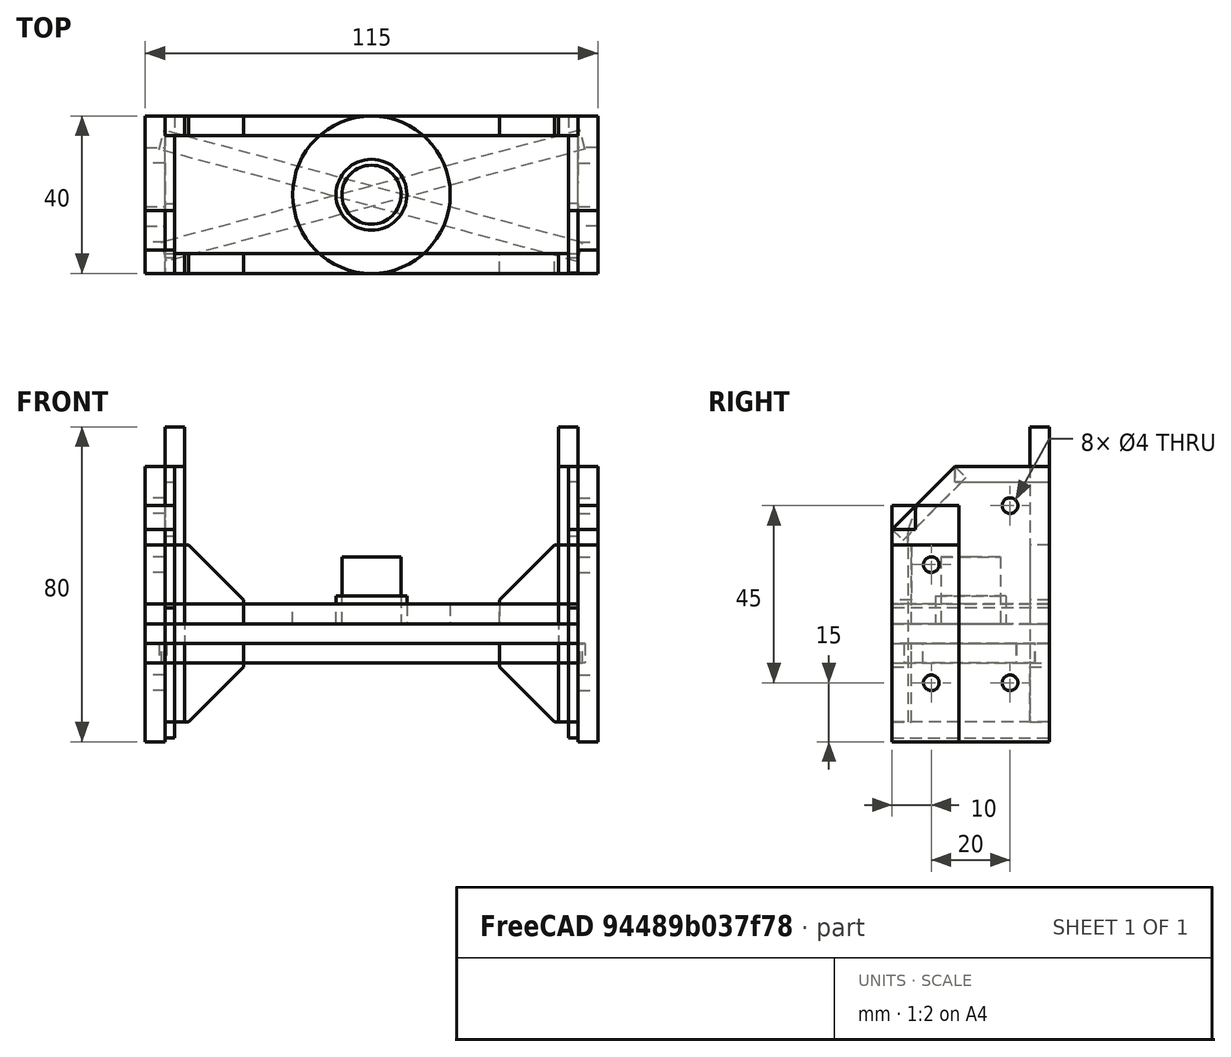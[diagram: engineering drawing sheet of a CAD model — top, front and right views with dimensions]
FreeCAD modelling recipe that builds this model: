
FCSTD DOCUMENT  (FreeCAD 0.20R29410 (Git))
Label: middle_01
License: All rights reserved
LicenseURL: http://en.wikipedia.org/wiki/All_rights_reserved
objects: Part::Extrusion×64, Part::Part2DObjectPython×61, Part::Cut×14, Part::Chamfer×13, Part::FeaturePython×6, Part::MultiFuse×4, App::FeaturePython×2
note: 162 computed .brp shape members not serialized (recipe doc carries the construction recipe); baked Part::Feature solids carry a one-line shape summary decoded from their .brp

FEATURE [Part::Part2DObjectPython] Rectangle003  # Draft 2D object (typed FeaturePython)
  Area = 0
  ChamferSize = 0
  Columns = 1
  FilletRadius = 0
  Height = 60
  Length = 17
  MakeFace = false
  Placement = pos=(0,0,10) rot=(0.57735,0.57735,0.57735;2.0944rad)
  Rows = 1
FEATURE [Part::Extrusion] Extrude002
  Base = -> Rectangle003
  Dir = (1,0,0)
  DirMode = 2
  FaceMakerClass = Part::FaceMakerBullseye
  LengthFwd = 5
  LengthRev = 0
  Placement = pos=(-140,0,0) rot=(0,0,1;0rad)
  Solid = true
  Symmetric = false
FEATURE [Part::Part2DObjectPython] Rectangle025  # Draft 2D object (typed FeaturePython)
  Area = 0
  ChamferSize = 0
  Columns = 1
  FilletRadius = 0
  Height = 60
  Length = 23
  MakeFace = false
  Placement = pos=(0,17,10) rot=(0.57735,0.57735,0.57735;2.0944rad)
  Rows = 1
FEATURE [Part::Extrusion] Extrude018
  Base = -> Rectangle025
  Dir = (1,-2e-16,2e-16)
  DirMode = 2
  FaceMakerClass = Part::FaceMakerBullseye
  LengthFwd = 5
  LengthRev = 0
  Placement = pos=(-140,0,0) rot=(0,0,1;0rad)
  Solid = true
  Symmetric = false
FEATURE [Part::Part2DObjectPython] Rectangle026  # Draft 2D object (typed FeaturePython)
  Area = 0
  ChamferSize = 0
  Columns = 1
  FilletRadius = 0
  Height = 20
  Length = 23
  MakeFace = false
  Placement = pos=(0,17,70) rot=(0.57735,0.57735,0.57735;2.0944rad)
  Rows = 1
FEATURE [Part::Extrusion] Extrude019
  Base = -> Rectangle026
  Dir = (1,-2e-16,2e-16)
  DirMode = 2
  FaceMakerClass = Part::FaceMakerBullseye
  LengthFwd = 5
  LengthRev = 0
  Placement = pos=(0,-17,0) rot=(0,0,1;0rad)
  Solid = true
  Symmetric = false
FEATURE [Part::Chamfer] Chamfer006
  Base = -> Extrude019
  Edges = 1 edges r=16: [Edge8]
  Placement = pos=(-140,0,0) rot=(0,0,1;0rad)
FEATURE [Part::Part2DObjectPython] Rectangle027  # Draft 2D object (typed FeaturePython)
  Area = 0
  ChamferSize = 0
  Columns = 1
  FilletRadius = 0
  Height = 20
  Length = 17
  MakeFace = false
  Placement = pos=(0,0,70) rot=(0.57735,0.57735,0.57735;2.0944rad)
  Rows = 1
FEATURE [Part::Extrusion] Extrude020
  Base = -> Rectangle027
  Dir = (1,-2e-16,2e-16)
  DirMode = 2
  FaceMakerClass = Part::FaceMakerBullseye
  LengthFwd = 5
  LengthRev = 0
  Placement = pos=(-140,23,0) rot=(0,0,1;0rad)
  Solid = true
  Symmetric = false
FEATURE [Part::Part2DObjectPython] Rectangle029  # Draft 2D object (typed FeaturePython)
  Area = 0
  ChamferSize = 0
  Columns = 1
  FilletRadius = 0
  Height = 4
  Length = 24
  MakeFace = false
  Placement = pos=(5,16,86) rot=(0.57735,0.57735,0.57735;2.0944rad)
  Rows = 1
FEATURE [Part::Part2DObjectPython] Rectangle028  # Draft 2D object (typed FeaturePython)
  Area = 0
  ChamferSize = 0
  Columns = 1
  FilletRadius = 0
  Height = 4
  Length = 22.6
  MakeFace = false
  Placement = pos=(5,2.85,71.15) rot=(0.678598,0.281085,0.678598;2.59356rad)
  Rows = 1
FEATURE [Part::Extrusion] Extrude033
  Base = -> Rectangle028
  Dir = (1,-2.79271e-06,1.15679e-06)
  DirMode = 2
  FaceMakerClass = Part::FaceMakerBullseye
  LengthFwd = 2.5
  LengthRev = 0
  Placement = pos=(-147.5,0,0) rot=(0,0,1;0rad)
  Solid = true
  Symmetric = false
FEATURE [Part::Extrusion] Extrude034
  Base = -> Rectangle029
  Dir = (1,-2e-16,2e-16)
  DirMode = 2
  FaceMakerClass = Part::FaceMakerBullseye
  LengthFwd = 2.5
  LengthRev = 0
  Placement = pos=(-147.5,0,0) rot=(0,0,1;0rad)
  Solid = true
  Symmetric = false
FEATURE [Part::Part2DObjectPython] Rectangle030  # Draft 2D object (typed FeaturePython)
  Area = 0
  ChamferSize = 0
  Columns = 1
  FilletRadius = 0
  Height = 4
  Length = 4
  MakeFace = false
  Placement = pos=(5,0,70) rot=(0.57735,0.57735,0.57735;2.0944rad)
  Rows = 1
FEATURE [Part::Extrusion] Extrude035
  Base = -> Rectangle030
  Dir = (1,-2e-16,2e-16)
  DirMode = 2
  FaceMakerClass = Part::FaceMakerBullseye
  LengthFwd = 2.5
  LengthRev = 0
  Placement = pos=(-147.5,0,0) rot=(0,0,1;0rad)
  Solid = true
  Symmetric = false
FEATURE [Part::FeaturePython] Facebinder012  # WARN: FeaturePython — macro-defined, semantics opaque (R4)
  Area = 10
  Extrusion = 0
  Faces = -> [Extrude035]
  RemoveSplitter = false
  Sew = false
FEATURE [Part::Extrusion] Extrude037
  Base = -> Facebinder012
  Dir = (2e-16,-1e-16,-1)
  DirMode = 2
  FaceMakerClass = Part::FaceMakerBullseye
  LengthFwd = 55
  LengthRev = 0
  Solid = false
  Symmetric = false
FEATURE [Part::Part2DObjectPython] Rectangle031  # Draft 2D object (typed FeaturePython)
  Area = 0
  ChamferSize = 0
  Columns = 1
  FilletRadius = 0
  Height = 4
  Length = 40
  MakeFace = false
  Placement = pos=(5,0,10) rot=(0.57735,0.57735,0.57735;2.0944rad)
  Rows = 1
FEATURE [Part::Extrusion] Extrude036
  Base = -> Rectangle031
  Dir = (1,-2e-16,2e-16)
  DirMode = 2
  FaceMakerClass = Part::FaceMakerBullseye
  LengthFwd = 2.5
  LengthRev = 0
  Placement = pos=(-147.5,0,30) rot=(0,0,1;0rad)
  Solid = true
  Symmetric = false
FEATURE [Part::Part2DObjectPython] Rectangle  # Draft 2D object (typed FeaturePython)
  Area = 0
  ChamferSize = 0
  Columns = 1
  FilletRadius = 0
  Height = 5
  Length = 40
  MakeFace = false
  Placement = pos=(-140,0,10) rot=(0.57735,0.57735,0.57735;2.0944rad)
  Rows = 1
FEATURE [Part::Extrusion] Extrude
  Base = -> Rectangle
  Dir = (1,-2e-16,2e-16)
  DirMode = 2
  FaceMakerClass = Part::FaceMakerBullseye
  LengthFwd = -110
  LengthRev = 0
  Placement = pos=(0,0,25) rot=(0,0,1;0rad)
  Solid = true
  Symmetric = false
FEATURE [Part::Part2DObjectPython] Rectangle032  # Draft 2D object (typed FeaturePython)
  Area = 0
  ChamferSize = 0
  Columns = 1
  FilletRadius = 0
  Height = 5
  Length = 5
  MakeFace = false
  Placement = pos=(-140,35,15) rot=(0.57735,0.57735,0.57735;2.0944rad)
  Rows = 1
FEATURE [Part::Part2DObjectPython] Rectangle033  # Draft 2D object (typed FeaturePython)
  Area = 0
  ChamferSize = 0
  Columns = 1
  FilletRadius = 0
  Height = 5
  Length = 5
  MakeFace = false
  Placement = pos=(-140,0,15) rot=(0.57735,0.57735,0.57735;2.0944rad)
  Rows = 1
FEATURE [Part::Extrusion] Extrude038
  Base = -> Rectangle032
  Dir = (1,-2e-16,2e-16)
  DirMode = 2
  FaceMakerClass = Part::FaceMakerBullseye
  LengthFwd = -110
  LengthRev = 0
  Placement = pos=(0,0,25) rot=(0,0,1;0rad)
  Solid = true
  Symmetric = false
FEATURE [Part::Extrusion] Extrude039
  Base = -> Rectangle033
  Dir = (1,-2e-16,2e-16)
  DirMode = 2
  FaceMakerClass = Part::FaceMakerBullseye
  LengthFwd = -110
  LengthRev = 0
  Placement = pos=(0,0,25) rot=(0,0,1;0rad)
  Solid = true
  Symmetric = false
FEATURE [Part::Part2DObjectPython] Rectangle034  # Draft 2D object (typed FeaturePython)
  Area = 0
  ChamferSize = 0
  Columns = 1
  FilletRadius = 0
  Height = 75
  Length = 5
  MakeFace = false
  Placement = pos=(-140,35,15) rot=(0.57735,0.57735,0.57735;2.0944rad)
  Rows = 1
FEATURE [Part::Extrusion] Extrude040
  Base = -> Rectangle034
  Dir = (1,0,0)
  DirMode = 2
  FaceMakerClass = Part::FaceMakerBullseye
  LengthFwd = -5
  LengthRev = 0
  Solid = true
  Symmetric = false
FEATURE [Part::Part2DObjectPython] Rectangle035  # Draft 2D object (typed FeaturePython)
  Area = 0
  ChamferSize = 0
  Columns = 1
  FilletRadius = 0
  Height = 20
  Length = 5
  MakeFace = false
  Placement = pos=(-145,35,15) rot=(0.57735,0.57735,0.57735;2.0944rad)
  Rows = 1
FEATURE [Part::Extrusion] Extrude041
  Base = -> Rectangle035
  Dir = (1,-2e-16,2e-16)
  DirMode = 2
  FaceMakerClass = Part::FaceMakerBullseye
  LengthFwd = -15
  LengthRev = 0
  Solid = true
  Symmetric = false
FEATURE [Part::Chamfer] Chamfer
  Base = -> Extrude041
  Edges = 1 edges r=14: [Edge10]
  Placement = pos=(0,0,25) rot=(0,0,1;0rad)
FEATURE [Part::Part2DObjectPython] Rectangle036  # Draft 2D object (typed FeaturePython)
  Area = 0
  ChamferSize = 0
  Columns = 1
  FilletRadius = 0
  Height = 20
  Length = 5
  MakeFace = false
  Placement = pos=(-145,35,15) rot=(0.57735,0.57735,0.57735;2.0944rad)
  Rows = 1
FEATURE [Part::Extrusion] Extrude042
  Base = -> Rectangle036
  Dir = (1,-2e-16,2e-16)
  DirMode = 2
  FaceMakerClass = Part::FaceMakerBullseye
  LengthFwd = -15
  LengthRev = 0
  Solid = true
  Symmetric = false
FEATURE [Part::Chamfer] Chamfer007
  Base = -> Extrude042
  Edges = 1 edges r=14: [Edge10]
  Placement = pos=(0,-35,25) rot=(0,0,1;0rad)
FEATURE [Part::FeaturePython] Facebinder  # WARN: FeaturePython — macro-defined, semantics opaque (R4)
  Area = 100
  Extrusion = 0
  Faces = -> [Chamfer007]
  RemoveSplitter = false
  Sew = false
FEATURE [Part::Extrusion] Extrude043
  Base = -> Facebinder
  Dir = (1,0,0)
  DirMode = 2
  FaceMakerClass = Part::FaceMakerBullseye
  LengthFwd = 5
  LengthRev = 0
  Solid = false
  Symmetric = false
FEATURE [Part::Part2DObjectPython] Rectangle037  # Draft 2D object (typed FeaturePython)
  Area = 0
  ChamferSize = 0
  Columns = 1
  FilletRadius = 0
  Height = 60
  Length = 23
  MakeFace = false
  Placement = pos=(0,17,10) rot=(0.57735,0.57735,0.57735;2.0944rad)
  Rows = 1
FEATURE [Part::Extrusion] Extrude044
  Base = -> Rectangle037
  Dir = (1,-2e-16,2e-16)
  DirMode = 2
  FaceMakerClass = Part::FaceMakerBullseye
  LengthFwd = 5
  LengthRev = 0
  Placement = pos=(-250,0,0) rot=(0,0,1;0rad)
  Solid = true
  Symmetric = false
FEATURE [Part::Part2DObjectPython] Rectangle038  # Draft 2D object (typed FeaturePython)
  Area = 0
  ChamferSize = 0
  Columns = 1
  FilletRadius = 0
  Height = 60
  Length = 17
  MakeFace = false
  Placement = pos=(0,0,10) rot=(0.57735,0.57735,0.57735;2.0944rad)
  Rows = 1
FEATURE [Part::Extrusion] Extrude045
  Base = -> Rectangle038
  Dir = (1,0,0)
  DirMode = 2
  FaceMakerClass = Part::FaceMakerBullseye
  LengthFwd = 5
  LengthRev = 0
  Placement = pos=(-250,0,0) rot=(0,0,1;0rad)
  Solid = true
  Symmetric = false
FEATURE [Part::Part2DObjectPython] Rectangle039  # Draft 2D object (typed FeaturePython)
  Area = 0
  ChamferSize = 0
  Columns = 1
  FilletRadius = 0
  Height = 20
  Length = 17
  MakeFace = false
  Placement = pos=(0,0,70) rot=(0.57735,0.57735,0.57735;2.0944rad)
  Rows = 1
FEATURE [Part::Extrusion] Extrude046
  Base = -> Rectangle039
  Dir = (1,-2e-16,2e-16)
  DirMode = 2
  FaceMakerClass = Part::FaceMakerBullseye
  LengthFwd = 5
  LengthRev = 0
  Placement = pos=(-250,23,0) rot=(0,0,1;0rad)
  Solid = true
  Symmetric = false
FEATURE [Part::Part2DObjectPython] Rectangle040  # Draft 2D object (typed FeaturePython)
  Area = 0
  ChamferSize = 0
  Columns = 1
  FilletRadius = 0
  Height = 20
  Length = 23
  MakeFace = false
  Placement = pos=(0,17,70) rot=(0.57735,0.57735,0.57735;2.0944rad)
  Rows = 1
FEATURE [Part::Extrusion] Extrude047
  Base = -> Rectangle040
  Dir = (1,-2e-16,2e-16)
  DirMode = 2
  FaceMakerClass = Part::FaceMakerBullseye
  LengthFwd = 5
  LengthRev = 0
  Placement = pos=(0,-17,0) rot=(0,0,1;0rad)
  Solid = true
  Symmetric = false
FEATURE [Part::Chamfer] Chamfer008
  Base = -> Extrude047
  Edges = 1 edges r=16: [Edge8]
  Placement = pos=(-250,0,0) rot=(0,0,1;0rad)
FEATURE [Part::Part2DObjectPython] Rectangle041  # Draft 2D object (typed FeaturePython)
  Area = 0
  ChamferSize = 0
  Columns = 1
  FilletRadius = 0
  Height = 4
  Length = 24
  MakeFace = false
  Placement = pos=(5,16,86) rot=(0.57735,0.57735,0.57735;2.0944rad)
  Rows = 1
FEATURE [Part::Extrusion] Extrude048
  Base = -> Rectangle041
  Dir = (1,-2e-16,2e-16)
  DirMode = 2
  FaceMakerClass = Part::FaceMakerBullseye
  LengthFwd = 2.5
  LengthRev = 0
  Placement = pos=(-250,0,0) rot=(0,0,1;0rad)
  Solid = true
  Symmetric = false
FEATURE [Part::Part2DObjectPython] Rectangle042  # Draft 2D object (typed FeaturePython)
  Area = 0
  ChamferSize = 0
  Columns = 1
  FilletRadius = 0
  Height = 4
  Length = 22.6
  MakeFace = false
  Placement = pos=(5,2.85,71.15) rot=(0.678598,0.281085,0.678598;2.59356rad)
  Rows = 1
FEATURE [Part::Extrusion] Extrude049
  Base = -> Rectangle042
  Dir = (1,-2.79271e-06,1.15679e-06)
  DirMode = 2
  FaceMakerClass = Part::FaceMakerBullseye
  LengthFwd = 2.5
  LengthRev = 0
  Placement = pos=(-250,0,0) rot=(0,0,1;0rad)
  Solid = true
  Symmetric = false
FEATURE [Part::Part2DObjectPython] Rectangle043  # Draft 2D object (typed FeaturePython)
  Area = 0
  ChamferSize = 0
  Columns = 1
  FilletRadius = 0
  Height = 4
  Length = 4
  MakeFace = false
  Placement = pos=(5,0,70) rot=(0.57735,0.57735,0.57735;2.0944rad)
  Rows = 1
FEATURE [Part::Extrusion] Extrude050
  Base = -> Rectangle043
  Dir = (1,-2e-16,2e-16)
  DirMode = 2
  FaceMakerClass = Part::FaceMakerBullseye
  LengthFwd = 2.5
  LengthRev = 0
  Placement = pos=(-250,0,0) rot=(0,0,1;0rad)
  Solid = true
  Symmetric = false
FEATURE [Part::Part2DObjectPython] Rectangle044  # Draft 2D object (typed FeaturePython)
  Area = 0
  ChamferSize = 0
  Columns = 1
  FilletRadius = 0
  Height = 4
  Length = 4
  MakeFace = false
  Placement = pos=(5,0,70) rot=(0.57735,0.57735,0.57735;2.0944rad)
  Rows = 1
FEATURE [Part::FeaturePython] Facebinder013  # WARN: FeaturePython — macro-defined, semantics opaque (R4)
  Area = 10
  Extrusion = 0
  RemoveSplitter = false
  Sew = false
FEATURE [Part::Extrusion] Extrude052
  Base = -> Facebinder013
  Dir = (2e-16,-1e-16,-1)
  DirMode = 2
  FaceMakerClass = Part::FaceMakerBullseye
  LengthFwd = 55
  LengthRev = 0
  Placement = pos=(-2.5,0,0) rot=(0,0,1;0rad)
  Solid = false
  Symmetric = false
FEATURE [Part::Part2DObjectPython] Rectangle045  # Draft 2D object (typed FeaturePython)
  Area = 0
  ChamferSize = 0
  Columns = 1
  FilletRadius = 0
  Height = 75
  Length = 5
  MakeFace = false
  Placement = pos=(-140,35,15) rot=(0.57735,0.57735,0.57735;2.0944rad)
  Rows = 1
FEATURE [Part::Extrusion] Extrude053
  Base = -> Rectangle045
  Dir = (1,0,0)
  DirMode = 2
  FaceMakerClass = Part::FaceMakerBullseye
  LengthFwd = -5
  LengthRev = 0
  Placement = pos=(-100,0,0) rot=(0,0,1;0rad)
  Solid = true
  Symmetric = false
FEATURE [Part::Part2DObjectPython] Rectangle046  # Draft 2D object (typed FeaturePython)
  Area = 0
  ChamferSize = 0
  Columns = 1
  FilletRadius = 0
  Height = 20
  Length = 5
  MakeFace = false
  Placement = pos=(-145,35,15) rot=(0.57735,0.57735,0.57735;2.0944rad)
  Rows = 1
FEATURE [Part::Extrusion] Extrude054
  Base = -> Rectangle046
  Dir = (1,-2e-16,2e-16)
  DirMode = 2
  FaceMakerClass = Part::FaceMakerBullseye
  LengthFwd = -15
  LengthRev = 0
  Solid = true
  Symmetric = false
FEATURE [Part::Chamfer] Chamfer009
  Base = -> Extrude054
  Edges = 1 edges r=14: [Edge10]
  Placement = pos=(0,-35,25) rot=(0,0,1;0rad)
FEATURE [Part::FeaturePython] Facebinder014  # WARN: FeaturePython — macro-defined, semantics opaque (R4)
  Area = 100
  Extrusion = 0
  Faces = -> [Chamfer009]
  RemoveSplitter = false
  Sew = false
FEATURE [Part::Extrusion] Extrude055
  Base = -> Facebinder014
  Dir = (1,0,0)
  DirMode = 2
  FaceMakerClass = Part::FaceMakerBullseye
  LengthFwd = 5
  LengthRev = 0
  Placement = pos=(-100,0,0) rot=(0,0,1;0rad)
  Solid = false
  Symmetric = false
FEATURE [Part::Part2DObjectPython] Rectangle047  # Draft 2D object (typed FeaturePython)
  Area = 0
  ChamferSize = 0
  Columns = 1
  FilletRadius = 0
  Height = 20
  Length = 5
  MakeFace = false
  Placement = pos=(-145,35,15) rot=(0.57735,0.57735,0.57735;2.0944rad)
  Rows = 1
FEATURE [Part::Part2DObjectPython] Rectangle048  # Draft 2D object (typed FeaturePython)
  Area = 0
  ChamferSize = 0
  Columns = 1
  FilletRadius = 0
  Height = 20
  Length = 5
  MakeFace = false
  Placement = pos=(-145,35,15) rot=(0.57735,0.57735,0.57735;2.0944rad)
  Rows = 1
FEATURE [Part::Extrusion] Extrude057
  Base = -> Rectangle048
  Dir = (1,-2e-16,2e-16)
  DirMode = 2
  FaceMakerClass = Part::FaceMakerBullseye
  LengthFwd = -15
  LengthRev = 0
  Placement = pos=(-80,0,0) rot=(0,0,1;0rad)
  Solid = true
  Symmetric = false
FEATURE [Part::Chamfer] Chamfer011
  Base = -> Extrude057
  Edges = 1 edges r=14: [Edge9]
  Placement = pos=(0,-35,25) rot=(0,0,1;0rad)
FEATURE [Part::Part2DObjectPython] Rectangle049  # Draft 2D object (typed FeaturePython)
  Area = 0
  ChamferSize = 0
  Columns = 1
  FilletRadius = 0
  Height = 20
  Length = 5
  MakeFace = false
  Placement = pos=(-145,35,15) rot=(0.57735,0.57735,0.57735;2.0944rad)
  Rows = 1
FEATURE [Part::Extrusion] Extrude058
  Base = -> Rectangle049
  Dir = (1,-2e-16,2e-16)
  DirMode = 2
  FaceMakerClass = Part::FaceMakerBullseye
  LengthFwd = -15
  LengthRev = 0
  Placement = pos=(-80,0,0) rot=(0,0,1;0rad)
  Solid = true
  Symmetric = false
FEATURE [Part::Chamfer] Chamfer012
  Base = -> Extrude058
  Edges = 1 edges r=14: [Edge9]
  Placement = pos=(0,0,25) rot=(0,0,1;0rad)
FEATURE [Part::Part2DObjectPython] Rectangle050  # Draft 2D object (typed FeaturePython)
  Area = 0
  ChamferSize = 0
  Columns = 1
  FilletRadius = 0
  Height = 4
  Length = 40
  MakeFace = false
  Placement = pos=(5,0,10) rot=(0.57735,0.57735,0.57735;2.0944rad)
  Rows = 1
FEATURE [Part::Extrusion] Extrude059
  Base = -> Rectangle050
  Dir = (1,-2e-16,2e-16)
  DirMode = 2
  FaceMakerClass = Part::FaceMakerBullseye
  LengthFwd = 2.5
  LengthRev = 0
  Placement = pos=(-250,0,30) rot=(0,0,1;0rad)
  Solid = true
  Symmetric = false
FEATURE [Part::Part2DObjectPython] Rectangle051  # Draft 2D object (typed FeaturePython)
  Area = 0
  ChamferSize = 0
  Columns = 1
  FilletRadius = 0
  Height = 4
  Length = 40
  MakeFace = false
  Placement = pos=(5,0,10) rot=(0.57735,0.57735,0.57735;2.0944rad)
  Rows = 1
FEATURE [Part::Extrusion] Extrude060
  Base = -> Rectangle051
  Dir = (1,-2e-16,2e-16)
  DirMode = 2
  FaceMakerClass = Part::FaceMakerBullseye
  LengthFwd = 2.5
  LengthRev = 0
  Placement = pos=(-147.5,0,1) rot=(0,0,1;0rad)
  Solid = true
  Symmetric = false
FEATURE [Part::Part2DObjectPython] Rectangle052  # Draft 2D object (typed FeaturePython)
  Area = 0
  ChamferSize = 0
  Columns = 1
  FilletRadius = 0
  Height = 4
  Length = 40
  MakeFace = false
  Placement = pos=(5,0,10) rot=(0.57735,0.57735,0.57735;2.0944rad)
  Rows = 1
FEATURE [Part::Extrusion] Extrude061
  Base = -> Rectangle052
  Dir = (1,-2e-16,2e-16)
  DirMode = 2
  FaceMakerClass = Part::FaceMakerBullseye
  LengthFwd = 2.5
  LengthRev = 0
  Placement = pos=(-250,0,1) rot=(0,0,1;0rad)
  Solid = true
  Symmetric = false
FEATURE [Part::Part2DObjectPython] Rectangle053  # Draft 2D object (typed FeaturePython)
  Area = 0
  ChamferSize = 0
  Columns = 1
  FilletRadius = 0
  Height = 20
  Length = 5
  MakeFace = false
  Placement = pos=(-145,35,15) rot=(0.57735,0.57735,0.57735;2.0944rad)
  Rows = 1
FEATURE [Part::Extrusion] Extrude062
  Base = -> Rectangle053
  Dir = (1,-2e-16,2e-16)
  DirMode = 2
  FaceMakerClass = Part::FaceMakerBullseye
  LengthFwd = -15
  LengthRev = 0
  Placement = pos=(2.5,-35,0) rot=(0,0,1;0rad)
  Solid = true
  Symmetric = false
FEATURE [Part::Chamfer] Chamfer013
  Base = -> Extrude062
  Edges = 1 edges r=14: [Edge4]
  Placement = pos=(-2.5,0,0) rot=(0,0,1;0rad)
FEATURE [Part::Part2DObjectPython] Rectangle054  # Draft 2D object (typed FeaturePython)
  Area = 0
  ChamferSize = 0
  Columns = 1
  FilletRadius = 0
  Height = 20
  Length = 5
  MakeFace = false
  Placement = pos=(-145,35,15) rot=(0.57735,0.57735,0.57735;2.0944rad)
  Rows = 1
FEATURE [Part::Extrusion] Extrude063
  Base = -> Rectangle054
  Dir = (1,-2e-16,2e-16)
  DirMode = 2
  FaceMakerClass = Part::FaceMakerBullseye
  LengthFwd = -15
  LengthRev = 0
  Placement = pos=(2.5,-35,0) rot=(0,0,1;0rad)
  Solid = true
  Symmetric = false
FEATURE [Part::Chamfer] Chamfer014
  Base = -> Extrude063
  Edges = 1 edges r=14: [Edge4]
  Placement = pos=(-2.5,35,0) rot=(0,0,1;0rad)
FEATURE [Part::Part2DObjectPython] Rectangle055  # Draft 2D object (typed FeaturePython)
  Area = 0
  ChamferSize = 0
  Columns = 1
  FilletRadius = 0
  Height = 20
  Length = 5
  MakeFace = false
  Placement = pos=(-145,35,15) rot=(0.57735,0.57735,0.57735;2.0944rad)
  Rows = 1
FEATURE [Part::Extrusion] Extrude064
  Base = -> Rectangle055
  Dir = (1,-2e-16,2e-16)
  DirMode = 2
  FaceMakerClass = Part::FaceMakerBullseye
  LengthFwd = -15
  LengthRev = 0
  Solid = true
  Symmetric = false
FEATURE [Part::Chamfer] Chamfer015
  Base = -> Extrude064
  Edges = 1 edges r=14: [Edge10]
  Placement = pos=(0,-35,25) rot=(0,0,1;0rad)
FEATURE [Part::FeaturePython] Facebinder015  # WARN: FeaturePython — macro-defined, semantics opaque (R4)
  Area = 100
  Extrusion = 0
  Faces = -> [Chamfer015]
  RemoveSplitter = false
  Sew = false
FEATURE [Part::Extrusion] Extrude065
  Base = -> Facebinder015
  Dir = (1,0,0)
  DirMode = 2
  FaceMakerClass = Part::FaceMakerBullseye
  LengthFwd = 5
  LengthRev = 0
  Placement = pos=(0,0,-25) rot=(0,0,1;0rad)
  Solid = false
  Symmetric = false
FEATURE [Part::Part2DObjectPython] Rectangle056  # Draft 2D object (typed FeaturePython)
  Area = 0
  ChamferSize = 0
  Columns = 1
  FilletRadius = 0
  Height = 20
  Length = 5
  MakeFace = false
  Placement = pos=(-145,35,15) rot=(0.57735,0.57735,0.57735;2.0944rad)
  Rows = 1
FEATURE [Part::Extrusion] Extrude066
  Base = -> Rectangle056
  Dir = (1,-2e-16,2e-16)
  DirMode = 2
  FaceMakerClass = Part::FaceMakerBullseye
  LengthFwd = -15
  LengthRev = 0
  Solid = true
  Symmetric = false
FEATURE [Part::Chamfer] Chamfer016
  Base = -> Extrude066
  Edges = 1 edges r=14: [Edge10]
  Placement = pos=(0,-35,25) rot=(0,0,1;0rad)
FEATURE [Part::FeaturePython] Facebinder016  # WARN: FeaturePython — macro-defined, semantics opaque (R4)
  Area = 100
  Extrusion = 0
  Faces = -> [Chamfer016]
  RemoveSplitter = false
  Sew = false
FEATURE [Part::Extrusion] Extrude067
  Base = -> Facebinder016
  Dir = (1,0,0)
  DirMode = 2
  FaceMakerClass = Part::FaceMakerBullseye
  LengthFwd = 5
  LengthRev = 0
  Placement = pos=(-100,0,-25) rot=(0,0,1;0rad)
  Solid = false
  Symmetric = false
FEATURE [Part::Part2DObjectPython] Rectangle057  # Draft 2D object (typed FeaturePython)
  Area = 0
  ChamferSize = 0
  Columns = 1
  FilletRadius = 0
  Height = 20
  Length = 5
  MakeFace = false
  Placement = pos=(-145,35,15) rot=(0.57735,0.57735,0.57735;2.0944rad)
  Rows = 1
FEATURE [Part::Extrusion] Extrude068
  Base = -> Rectangle057
  Dir = (1,-2e-16,2e-16)
  DirMode = 2
  FaceMakerClass = Part::FaceMakerBullseye
  LengthFwd = -15
  LengthRev = 0
  Placement = pos=(-80,-35,0) rot=(0,0,1;0rad)
  Solid = true
  Symmetric = false
FEATURE [Part::Chamfer] Chamfer017
  Base = -> Extrude068
  Edges = 1 edges r=14: [Edge3]
FEATURE [Part::Part2DObjectPython] Rectangle058  # Draft 2D object (typed FeaturePython)
  Area = 0
  ChamferSize = 0
  Columns = 1
  FilletRadius = 0
  Height = 20
  Length = 5
  MakeFace = false
  Placement = pos=(-145,35,15) rot=(0.57735,0.57735,0.57735;2.0944rad)
  Rows = 1
FEATURE [Part::Extrusion] Extrude069
  Base = -> Rectangle058
  Dir = (1,-2e-16,2e-16)
  DirMode = 2
  FaceMakerClass = Part::FaceMakerBullseye
  LengthFwd = -15
  LengthRev = 0
  Placement = pos=(-80,-35,0) rot=(0,0,1;0rad)
  Solid = true
  Symmetric = false
FEATURE [Part::Chamfer] Chamfer018
  Base = -> Extrude069
  Edges = 1 edges r=14: [Edge3]
  Placement = pos=(0,35,0) rot=(0,0,1;0rad)
FEATURE [Part::Part2DObjectPython] Rectangle059  # Draft 2D object (typed FeaturePython)
  Area = 0
  ChamferSize = 0
  Columns = 1
  FilletRadius = 0
  Height = 5
  Length = 5
  MakeFace = false
  Placement = pos=(-140,0,15) rot=(0.57735,0.57735,0.57735;2.0944rad)
  Rows = 1
FEATURE [Part::Extrusion] Extrude070
  Base = -> Rectangle059
  Dir = (1,-2e-16,2e-16)
  DirMode = 2
  FaceMakerClass = Part::FaceMakerBullseye
  LengthFwd = -110
  LengthRev = 0
  Placement = pos=(0,0,15) rot=(0,0,1;0rad)
  Solid = true
  Symmetric = false
FEATURE [Part::Part2DObjectPython] Rectangle060  # Draft 2D object (typed FeaturePython)
  Area = 0
  ChamferSize = 0
  Columns = 1
  FilletRadius = 0
  Height = 5
  Length = 5
  MakeFace = false
  Placement = pos=(-140,35,15) rot=(0.57735,0.57735,0.57735;2.0944rad)
  Rows = 1
FEATURE [Part::Extrusion] Extrude071
  Base = -> Rectangle060
  Dir = (1,-2e-16,2e-16)
  DirMode = 2
  FaceMakerClass = Part::FaceMakerBullseye
  LengthFwd = -110
  LengthRev = 0
  Placement = pos=(0,0,15) rot=(0,0,1;0rad)
  Solid = true
  Symmetric = false
FEATURE [Part::Part2DObjectPython] Rectangle061  # Draft 2D object (typed FeaturePython)
  Area = 0
  ChamferSize = 0
  Columns = 1
  FilletRadius = 0
  Height = 5
  Length = 5
  MakeFace = false
  Placement = pos=(-140,35,15) rot=(0.57735,0.57735,0.57735;2.0944rad)
  Rows = 1
FEATURE [Part::Extrusion] Extrude072
  Base = -> Rectangle061
  Dir = (1,-2e-16,2e-16)
  DirMode = 2
  FaceMakerClass = Part::FaceMakerBullseye
  LengthFwd = -110
  LengthRev = 0
  Placement = pos=(6,34,15) rot=(0,0,1;0.261799rad)
  Solid = true
  Symmetric = false
FEATURE [Part::Part2DObjectPython] Rectangle062  # Draft 2D object (typed FeaturePython)
  Area = 0
  ChamferSize = 0
  Columns = 1
  FilletRadius = 0
  Height = 5
  Length = 5
  MakeFace = false
  Placement = pos=(-140,35,15) rot=(0.57735,0.57735,0.57735;2.0944rad)
  Rows = 1
FEATURE [Part::Extrusion] Extrude073
  Base = -> Rectangle062
  Dir = (1,0,0)
  DirMode = 2
  FaceMakerClass = Part::FaceMakerBullseye
  LengthFwd = -110
  LengthRev = 0
  Placement = pos=(-14,-67,15) rot=(0,0,-1;0.261799rad)
  Solid = true
  Symmetric = false
FEATURE [Part::Part2DObjectPython] Circle  # Draft 2D object (typed FeaturePython)
  Area = 0
  FirstAngle = 0
  LastAngle = 0
  MakeFace = false
  Placement = pos=(-192.5,20,40) rot=(0,0,1;3.14159rad)
  Radius = 20
FEATURE [Part::Part2DObjectPython] Circle001  # Draft 2D object (typed FeaturePython)
  Area = 0
  FirstAngle = 0
  LastAngle = 0
  MakeFace = false
  Placement = pos=(-192.5,20,40) rot=(0,0,1;3.14159rad)
  Radius = 9
FEATURE [Part::Part2DObjectPython] Circle002  # Draft 2D object (typed FeaturePython)
  Area = 0
  FirstAngle = 0
  LastAngle = 0
  MakeFace = false
  Placement = pos=(-192.5,20,40) rot=(0,0,1;3.14159rad)
  Radius = 7.5
FEATURE [App::FeaturePython] Dimension  # Draft dimension (typed FeaturePython)
  Diameter = true
  Dimline = (-198.431,14.2821,40)
  Direction = (0,0,0)
  Distance = 15
  End = (-197.899,14.7945,40)
  LinkedGeometry = -> [Circle002]
  Normal = (-2e-16,1e-16,1)
  Start = (-187.101,25.2055,40)
  Support = -> Circle002
FEATURE [App::FeaturePython] Dimension001  # Draft dimension (typed FeaturePython)
  Diameter = true
  Dimline = (-166.158,20.0492,40)
  Direction = (0,0,0)
  Distance = 40
  End = (-172.5,20.0374,40)
  LinkedGeometry = -> [Circle]
  Normal = (-2e-16,1e-16,1)
  Start = (-212.5,19.9626,40)
  Support = -> Circle
FEATURE [Part::Extrusion] Extrude074
  Base = -> Circle
  Dir = (-2e-16,1e-16,1)
  DirMode = 2
  FaceMakerClass = Part::FaceMakerBullseye
  LengthFwd = 5
  LengthRev = 0
  Solid = true
  Symmetric = false
FEATURE [Part::Extrusion] Extrude075
  Base = -> Circle001
  Dir = (0,0,1)
  DirMode = 2
  FaceMakerClass = Part::FaceMakerBullseye
  LengthFwd = 7
  LengthRev = 0
  Solid = true
  Symmetric = false
FEATURE [Part::Extrusion] Extrude076
  Base = -> Circle002
  Dir = (0,0,1)
  DirMode = 2
  FaceMakerClass = Part::FaceMakerBullseye
  LengthFwd = 17
  LengthRev = 0
  Solid = true
  Symmetric = false
FEATURE [Part::MultiFuse] Fusion
  Placement = pos=(0,0,-10) rot=(0,0,1;0rad)
  Shapes = -> [Extrude020,Chamfer006,Extrude033,Extrude034,Extrude035]
FEATURE [Part::MultiFuse] Fusion001
  Placement = pos=(0,0,-10) rot=(0,0,1;0rad)
  Shapes = -> [Chamfer008,Extrude046,Extrude048,Extrude049,Extrude050]
FEATURE [Part::Part2DObjectPython] Rectangle063  # Draft 2D object (typed FeaturePython)
  Area = 0
  ChamferSize = 0
  Columns = 1
  FilletRadius = 0
  Height = 6
  Length = 6
  MakeFace = false
  Placement = pos=(-250,6,64) rot=(0.57735,-0.57735,-0.57735;2.0944rad)
  Rows = 1
FEATURE [Part::Extrusion] Extrude077
  Base = -> Rectangle063
  Dir = (-1,-2e-16,2e-16)
  DirMode = 2
  FaceMakerClass = Part::FaceMakerBullseye
  LengthFwd = -7.5
  LengthRev = 0
  Solid = true
  Symmetric = false
FEATURE [Part::Part2DObjectPython] Rectangle064  # Draft 2D object (typed FeaturePython)
  Area = 0
  ChamferSize = 0
  Columns = 1
  FilletRadius = 0
  Height = 6
  Length = 6
  MakeFace = false
  Placement = pos=(-250,6,64) rot=(0.57735,-0.57735,-0.57735;2.0944rad)
  Rows = 1
FEATURE [Part::Extrusion] Extrude078
  Base = -> Rectangle064
  Dir = (-1,-2e-16,2e-16)
  DirMode = 2
  FaceMakerClass = Part::FaceMakerBullseye
  LengthFwd = -7.5
  LengthRev = 0
  Solid = true
  Symmetric = false
FEATURE [Part::Cut] Cut
  Base = -> Extrude045
  Tool = -> Extrude078
FEATURE [Part::Part2DObjectPython] Rectangle065  # Draft 2D object (typed FeaturePython)
  Area = 0
  ChamferSize = 0
  Columns = 1
  FilletRadius = 0
  Height = 6
  Length = 6
  MakeFace = false
  Placement = pos=(-250,6,64) rot=(0.57735,-0.57735,-0.57735;2.0944rad)
  Rows = 1
FEATURE [Part::Extrusion] Extrude079
  Base = -> Rectangle065
  Dir = (-1,-2e-16,2e-16)
  DirMode = 2
  FaceMakerClass = Part::FaceMakerBullseye
  LengthFwd = -7.5
  LengthRev = 0
  Solid = true
  Symmetric = false
FEATURE [Part::Cut] Cut001
  Base = -> Extrude052
  Tool = -> Extrude079
FEATURE [Part::Part2DObjectPython] Rectangle066  # Draft 2D object (typed FeaturePython)
  Area = 0
  ChamferSize = 0
  Columns = 1
  FilletRadius = 0
  Height = 6
  Length = 6
  MakeFace = false
  Placement = pos=(-250,6,64) rot=(0.57735,-0.57735,-0.57735;2.0944rad)
  Rows = 1
FEATURE [Part::Extrusion] Extrude080
  Base = -> Rectangle066
  Dir = (-1,-2e-16,2e-16)
  DirMode = 2
  FaceMakerClass = Part::FaceMakerBullseye
  LengthFwd = -7.5
  LengthRev = 0
  Placement = pos=(107.5,0,0) rot=(0,0,1;0rad)
  Solid = true
  Symmetric = false
FEATURE [Part::Part2DObjectPython] Rectangle067  # Draft 2D object (typed FeaturePython)
  Area = 0
  ChamferSize = 0
  Columns = 1
  FilletRadius = 0
  Height = 6
  Length = 6
  MakeFace = false
  Placement = pos=(-250,6,64) rot=(0.57735,-0.57735,-0.57735;2.0944rad)
  Rows = 1
FEATURE [Part::Extrusion] Extrude081
  Base = -> Rectangle067
  Dir = (-1,-2e-16,2e-16)
  DirMode = 2
  FaceMakerClass = Part::FaceMakerBullseye
  LengthFwd = -7.5
  LengthRev = 0
  Placement = pos=(107.5,0,0) rot=(0,0,1;0rad)
  Solid = true
  Symmetric = false
FEATURE [Part::Cut] Cut002
  Base = -> Extrude002
  Tool = -> Extrude080
FEATURE [Part::Cut] Cut003
  Base = -> Extrude037
  Tool = -> Extrude081
FEATURE [Part::Part2DObjectPython] Rectangle068  # Draft 2D object (typed FeaturePython)
  Area = 0
  ChamferSize = 0
  Columns = 1
  FilletRadius = 0
  Height = 10
  Length = 5
  MakeFace = false
  Placement = pos=(-245,40,80) rot=(0.57735,-0.57735,-0.57735;2.0944rad)
  Rows = 1
FEATURE [Part::Extrusion] Extrude082
  Base = -> Rectangle068
  Dir = (-1,-2e-16,2e-16)
  DirMode = 2
  FaceMakerClass = Part::FaceMakerBullseye
  LengthFwd = -5
  LengthRev = 0
  Solid = true
  Symmetric = false
FEATURE [Part::Part2DObjectPython] Rectangle069  # Draft 2D object (typed FeaturePython)
  Area = 0
  ChamferSize = 0
  Columns = 1
  FilletRadius = 0
  Height = 10
  Length = 5
  MakeFace = false
  Placement = pos=(-245,40,80) rot=(0.57735,-0.57735,-0.57735;2.0944rad)
  Rows = 1
FEATURE [Part::Extrusion] Extrude083
  Base = -> Rectangle069
  Dir = (-1,-2e-16,2e-16)
  DirMode = 2
  FaceMakerClass = Part::FaceMakerBullseye
  LengthFwd = -5
  LengthRev = 0
  Solid = true
  Symmetric = false
FEATURE [Part::Cut] Cut004
  Base = -> Extrude053
  Tool = -> Extrude083
FEATURE [Part::Part2DObjectPython] Rectangle070  # Draft 2D object (typed FeaturePython)
  Area = 0
  ChamferSize = 0
  Columns = 1
  FilletRadius = 0
  Height = 10
  Length = 5
  MakeFace = false
  Placement = pos=(-245,40,80) rot=(0.57735,-0.57735,-0.57735;2.0944rad)
  Rows = 1
FEATURE [Part::Extrusion] Extrude084
  Base = -> Rectangle070
  Dir = (-1,-2e-16,2e-16)
  DirMode = 2
  FaceMakerClass = Part::FaceMakerBullseye
  LengthFwd = -5
  LengthRev = 0
  Placement = pos=(100,0,0) rot=(0,0,1;0rad)
  Solid = true
  Symmetric = false
FEATURE [Part::Part2DObjectPython] Rectangle071  # Draft 2D object (typed FeaturePython)
  Area = 0
  ChamferSize = 0
  Columns = 1
  FilletRadius = 0
  Height = 10
  Length = 5
  MakeFace = false
  Placement = pos=(-245,40,80) rot=(0.57735,-0.57735,-0.57735;2.0944rad)
  Rows = 1
FEATURE [Part::Extrusion] Extrude085
  Base = -> Rectangle071
  Dir = (-1,-2e-16,2e-16)
  DirMode = 2
  FaceMakerClass = Part::FaceMakerBullseye
  LengthFwd = -5
  LengthRev = 0
  Placement = pos=(100,0,0) rot=(0,0,1;0rad)
  Solid = true
  Symmetric = false
FEATURE [Part::Cut] Cut005
  Base = -> Extrude040
  Tool = -> Extrude085
FEATURE [Part::Part2DObjectPython] Rectangle072  # Draft 2D object (typed FeaturePython)
  Area = 150
  ChamferSize = 0
  Columns = 1
  FilletRadius = 0
  Height = 15
  Length = 10
  MakeFace = true
  Placement = pos=(-135,40,10) rot=(0.57735,-0.57735,-0.57735;2.0944rad)
  Rows = 1
FEATURE [Part::Part2DObjectPython] Circle003  # Draft 2D object (typed FeaturePython)
  Area = 12.5664
  FirstAngle = 0
  LastAngle = 0
  MakeFace = true
  Placement = pos=(-135,30,25) rot=(0.57735,0.57735,0.57735;2.0944rad)
  Radius = 2
FEATURE [Part::Part2DObjectPython] Circle004  # Draft 2D object (typed FeaturePython)
  Area = 12.5664
  FirstAngle = 0
  LastAngle = 0
  MakeFace = true
  Placement = pos=(-135,30,70) rot=(0.57735,0.57735,0.57735;2.0944rad)
  Radius = 2
FEATURE [Part::Part2DObjectPython] Circle005  # Draft 2D object (typed FeaturePython)
  Area = 12.5664
  FirstAngle = 0
  LastAngle = 0
  MakeFace = true
  Placement = pos=(-250,10,25) rot=(0.57735,0.57735,0.57735;2.0944rad)
  Radius = 2
FEATURE [Part::Part2DObjectPython] Circle006  # Draft 2D object (typed FeaturePython)
  Area = 12.5664
  FirstAngle = 0
  LastAngle = 0
  MakeFace = true
  Placement = pos=(-135,10,55) rot=(0.57735,0.57735,0.57735;2.0944rad)
  Radius = 2
FEATURE [Part::Part2DObjectPython] Circle007  # Draft 2D object (typed FeaturePython)
  Area = 12.5664
  FirstAngle = 0
  LastAngle = 0
  MakeFace = true
  Placement = pos=(-250,30,25) rot=(0.57735,0.57735,0.57735;2.0944rad)
  Radius = 2
FEATURE [Part::Part2DObjectPython] Circle008  # Draft 2D object (typed FeaturePython)
  Area = 12.5664
  FirstAngle = 0
  LastAngle = 0
  MakeFace = true
  Placement = pos=(-135,10,25) rot=(0.57735,0.57735,0.57735;2.0944rad)
  Radius = 2
FEATURE [Part::Part2DObjectPython] Circle009  # Draft 2D object (typed FeaturePython)
  Area = 12.5664
  FirstAngle = 0
  LastAngle = 0
  MakeFace = true
  Placement = pos=(-250,30,70) rot=(0.57735,0.57735,0.57735;2.0944rad)
  Radius = 2
FEATURE [Part::Part2DObjectPython] Circle010  # Draft 2D object (typed FeaturePython)
  Area = 12.5664
  FirstAngle = 0
  LastAngle = 0
  MakeFace = true
  Placement = pos=(-250,10,55) rot=(0.57735,0.57735,0.57735;2.0944rad)
  Radius = 2
FEATURE [Part::Extrusion] Extrude086
  Base = -> Circle008
  Dir = (1,0,0)
  DirMode = 2
  FaceMakerClass = Part::FaceMakerBullseye
  LengthFwd = -5
  LengthRev = 0
  Solid = false
  Symmetric = false
FEATURE [Part::Extrusion] Extrude087
  Base = -> Circle003
  Dir = (1,0,0)
  DirMode = 2
  FaceMakerClass = Part::FaceMakerBullseye
  LengthFwd = -5
  LengthRev = 0
  Solid = false
  Symmetric = false
FEATURE [Part::Extrusion] Extrude088
  Base = -> Circle004
  Dir = (1,-2e-16,2e-16)
  DirMode = 2
  FaceMakerClass = Part::FaceMakerBullseye
  LengthFwd = -5
  LengthRev = 0
  Solid = false
  Symmetric = false
FEATURE [Part::Extrusion] Extrude089
  Base = -> Circle006
  Dir = (1,-2e-16,2e-16)
  DirMode = 2
  FaceMakerClass = Part::FaceMakerBullseye
  LengthFwd = -5
  LengthRev = 0
  Solid = false
  Symmetric = false
FEATURE [Part::MultiFuse] Fusion002
  Shapes = -> [Extrude018,Fusion]
FEATURE [Part::Cut] Cut006
  Base = -> Fusion002
  Tool = -> Extrude088
FEATURE [Part::Cut] Cut007
  Base = -> Cut002
  Tool = -> Extrude089
FEATURE [Part::Cut] Cut008
  Base = -> Cut006
  Tool = -> Extrude087
FEATURE [Part::Cut] Cut009
  Base = -> Cut007
  Tool = -> Extrude086
FEATURE [Part::Extrusion] Extrude090
  Base = -> Circle007
  Dir = (1,-2e-16,2e-16)
  DirMode = 2
  FaceMakerClass = Part::FaceMakerBullseye
  LengthFwd = 5
  LengthRev = 0
  Solid = false
  Symmetric = false
FEATURE [Part::Extrusion] Extrude091
  Base = -> Circle005
  Dir = (1,-2e-16,2e-16)
  DirMode = 2
  FaceMakerClass = Part::FaceMakerBullseye
  LengthFwd = 5
  LengthRev = 0
  Solid = false
  Symmetric = false
FEATURE [Part::Extrusion] Extrude092
  Base = -> Circle009
  Dir = (1,-2e-16,2e-16)
  DirMode = 2
  FaceMakerClass = Part::FaceMakerBullseye
  LengthFwd = 5
  LengthRev = 0
  Solid = false
  Symmetric = false
FEATURE [Part::Extrusion] Extrude093
  Base = -> Circle010
  Dir = (1,-2e-16,2e-16)
  DirMode = 2
  FaceMakerClass = Part::FaceMakerBullseye
  LengthFwd = 5
  LengthRev = 0
  Solid = false
  Symmetric = false
FEATURE [Part::Cut] Cut010
  Base = -> Cut
  Tool = -> Extrude091
FEATURE [Part::Cut] Cut011
  Base = -> Cut010
  Tool = -> Extrude093
FEATURE [Part::Cut] Cut012
  Base = -> Extrude044
  Tool = -> Extrude090
FEATURE [Part::MultiFuse] Fusion003
  Shapes = -> [Fusion001,Cut012]
FEATURE [Part::Cut] Cut013
  Base = -> Fusion003
  Tool = -> Extrude092
